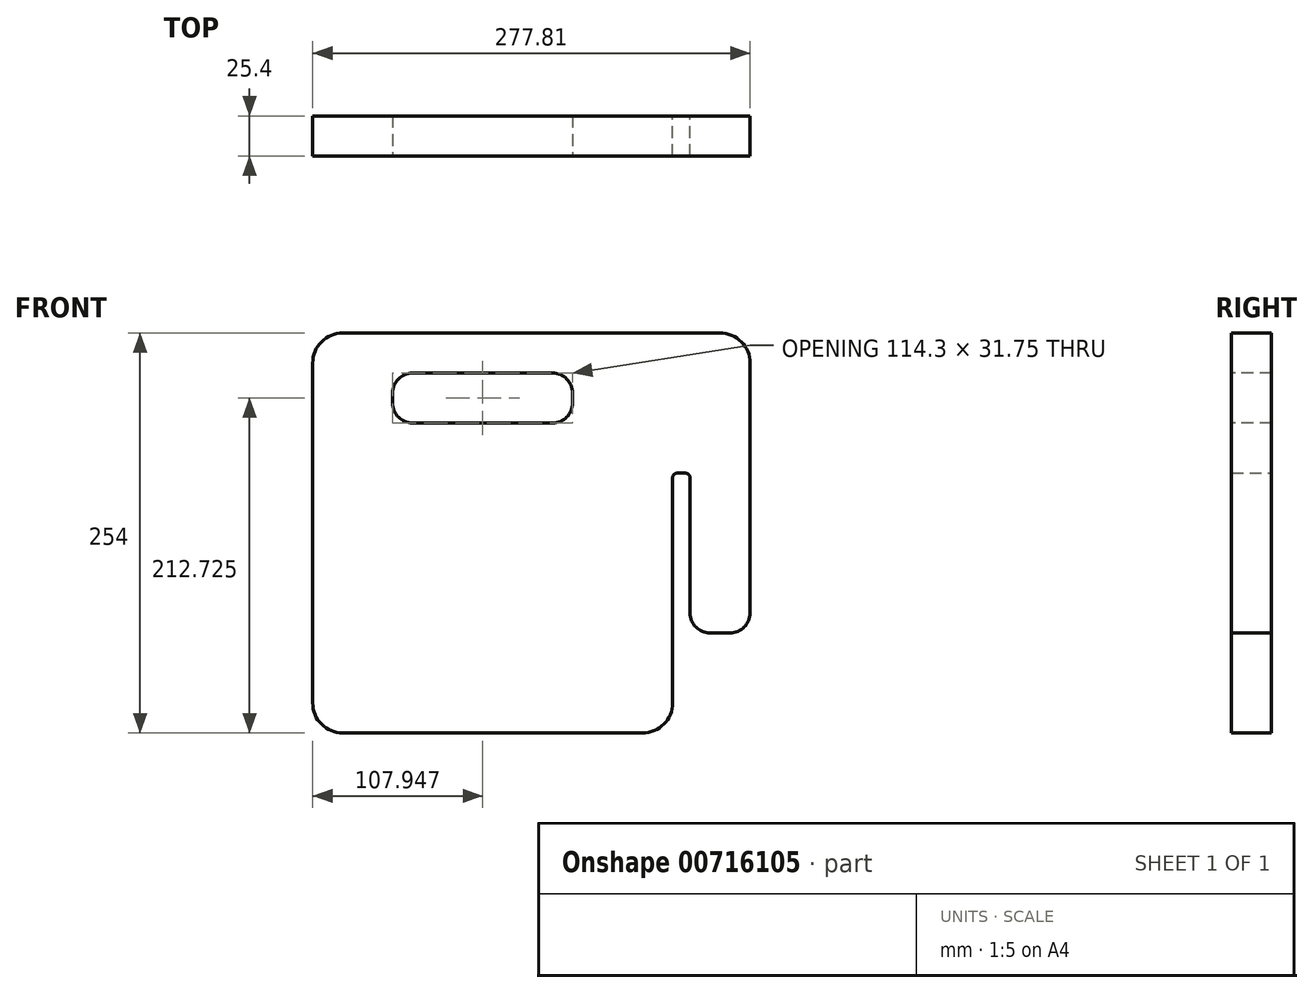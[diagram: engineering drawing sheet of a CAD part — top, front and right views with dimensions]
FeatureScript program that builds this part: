
annotation { "Feature Type Name" : "Feature", "Feature Type Description" : "" }
export const myFeature = defineFeature(function(context is Context, id is Id, definition is map)
    precondition{}
    {
        {
            var Q0;
            Q0=qCreatedBy(makeId("Front.planeOp"),FACE);
            var sketch = newSketch(context, id + "F0", { "sketchPlane" : qUnion([Q0])});
            skLineSegment(sketch, "E0.bottom", {"start": v(-69.16, 190.5) * mm, "end": v(170.55, 190.5) * mm});
            skLineSegment(sketch, "E0.left", {"start": v(-88.21, 171.45) * mm, "end": v(-88.21, -44.45) * mm});
            skLineSegment(sketch, "E1", {"start": v(148.32, 101.6) * mm, "end": v(143.56, 101.6) * mm});
            skLineSegment(sketch, "E2", {"start": v(140.39, 98.43) * mm, "end": v(140.39, -44.45) * mm});
            skLineSegment(sketch, "E3", {"start": v(-69.16, -63.5) * mm, "end": v(121.34, -63.5) * mm});
            skLineSegment(sketch, "E4", {"start": v(164.2, 0) * mm, "end": v(176.9, 0) * mm});
            skLineSegment(sketch, "E5", {"start": v(151.5, 12.7) * mm, "end": v(151.5, 98.43) * mm});
            skLineSegment(sketch, "E6", {"start": v(189.6, 12.7) * mm, "end": v(189.6, 171.45) * mm});
            skPoint(sketch, "E7.visualSharp", {"position": v(-88.21, 190.5) * mm});
            skArc(sketch, "E7.filletArc", {"start": v(-69.16, 190.5) * mm, "mid": v(-82.63, 184.92) * mm, "end": v(-88.21, 171.45) * mm});
            skPoint(sketch, "E8.visualSharp", {"position": v(-88.21, -63.5) * mm});
            skArc(sketch, "E8.filletArc", {"start": v(-88.21, -44.45) * mm, "mid": v(-82.63, -57.92) * mm, "end": v(-69.16, -63.5) * mm});
            skPoint(sketch, "E9.visualSharp", {"position": v(189.6, 190.5) * mm});
            skArc(sketch, "E9.filletArc", {"start": v(189.6, 171.45) * mm, "mid": v(184.02, 184.92) * mm, "end": v(170.55, 190.5) * mm});
            skPoint(sketch, "E10.visualSharp", {"position": v(189.6, 0) * mm});
            skArc(sketch, "E10.filletArc", {"start": v(176.9, 0) * mm, "mid": v(185.88, 3.72) * mm, "end": v(189.6, 12.7) * mm});
            skPoint(sketch, "E11.visualSharp", {"position": v(151.5, 0) * mm});
            skArc(sketch, "E11.filletArc", {"start": v(151.5, 12.7) * mm, "mid": v(155.22, 3.72) * mm, "end": v(164.2, 0) * mm});
            skPoint(sketch, "E12.visualSharp", {"position": v(140.39, -63.5) * mm});
            skArc(sketch, "E12.filletArc", {"start": v(121.34, -63.5) * mm, "mid": v(134.8, -57.92) * mm, "end": v(140.39, -44.45) * mm});
            skPoint(sketch, "E13.visualSharp", {"position": v(151.5, 101.6) * mm});
            skArc(sketch, "E13.filletArc", {"start": v(151.5, 98.43) * mm, "mid": v(150.57, 100.67) * mm, "end": v(148.32, 101.6) * mm});
            skPoint(sketch, "E14.visualSharp", {"position": v(140.39, 101.6) * mm});
            skArc(sketch, "E14.filletArc", {"start": v(143.56, 101.6) * mm, "mid": v(141.32, 100.67) * mm, "end": v(140.39, 98.43) * mm});
            skSolve(sketch);
        }
        {
            var Q0;
            Q0=makeQuery(id+"F0.imprint","IMPRINT",FACE,{"disambiguationData":[TD([[makeQuery(id+"F0.imprint","IMPRINT",EDGE,{"derivedFrom":sQuery(id+"F0.wireOp",EDGE,"E0.bottom")}),-1.0]])]});
            extrude(context, id + "F1", {"entities" : qUnion([Q0]), "depth" : 25.4 * mm, "offsetDistance" : 25.4 * mm});
        }
        {
            var Q0;
            Q0=makeQuery(id+"F1.opExtrude","CAP_FACE",FACE,{"disambiguationData":[OSD([sQuery(id+"F0.wireOp",EDGE,"E0.bottom"),sQuery(id+"F0.wireOp",EDGE,"E0.left"),sQuery(id+"F0.wireOp",EDGE,"E1"),sQuery(id+"F0.wireOp",EDGE,"E2"),sQuery(id+"F0.wireOp",EDGE,"E3"),sQuery(id+"F0.wireOp",EDGE,"E4"),sQuery(id+"F0.wireOp",EDGE,"E5"),sQuery(id+"F0.wireOp",EDGE,"E6"),sQuery(id+"F0.wireOp",EDGE,"E7.filletArc"),sQuery(id+"F0.wireOp",EDGE,"E8.filletArc"),sQuery(id+"F0.wireOp",EDGE,"E9.filletArc"),sQuery(id+"F0.wireOp",EDGE,"E10.filletArc"),sQuery(id+"F0.wireOp",EDGE,"E11.filletArc"),sQuery(id+"F0.wireOp",EDGE,"E12.filletArc"),sQuery(id+"F0.wireOp",EDGE,"E13.filletArc"),sQuery(id+"F0.wireOp",EDGE,"E14.filletArc")])],"isStart":false});
            var sketch = newSketch(context, id + "F2", { "sketchPlane" : qUnion([Q0])});
            skLineSegment(sketch, "E15.bottom", {"start": v(-24.71, 165.1) * mm, "end": v(64.19, 165.1) * mm});
            skLineSegment(sketch, "E15.top", {"start": v(-24.71, 133.35) * mm, "end": v(64.19, 133.35) * mm});
            skLineSegment(sketch, "E15.left", {"start": v(-37.41, 152.4) * mm, "end": v(-37.41, 146.05) * mm});
            skLineSegment(sketch, "E15.right", {"start": v(76.89, 152.4) * mm, "end": v(76.89, 146.05) * mm});
            skPoint(sketch, "E16.visualSharp", {"position": v(-37.41, 165.1) * mm});
            skArc(sketch, "E16.filletArc", {"start": v(-24.71, 165.1) * mm, "mid": v(-33.7, 161.38) * mm, "end": v(-37.41, 152.4) * mm});
            skPoint(sketch, "E17.visualSharp", {"position": v(-37.41, 133.35) * mm});
            skArc(sketch, "E17.filletArc", {"start": v(-37.41, 146.05) * mm, "mid": v(-33.7, 137.07) * mm, "end": v(-24.71, 133.35) * mm});
            skPoint(sketch, "E18.visualSharp", {"position": v(76.89, 133.35) * mm});
            skArc(sketch, "E18.filletArc", {"start": v(64.19, 133.35) * mm, "mid": v(73.17, 137.07) * mm, "end": v(76.89, 146.05) * mm});
            skPoint(sketch, "E19.visualSharp", {"position": v(76.89, 165.1) * mm});
            skArc(sketch, "E19.filletArc", {"start": v(76.89, 152.4) * mm, "mid": v(73.17, 161.38) * mm, "end": v(64.19, 165.1) * mm});
            skSolve(sketch);
        }
        {
            var Q0;
            Q0=makeQuery(id+"F2.imprint","IMPRINT",FACE,{"disambiguationData":[TD([[makeQuery(id+"F2.imprint","IMPRINT",EDGE,{"derivedFrom":sQuery(id+"F2.wireOp",EDGE,"E15.bottom")}),-1.0]])]});
            extrude(context, id + "F3", {"entities" : qUnion([Q0]), "operationType" : NewBodyOperationType.REMOVE, "endBound" : BoundingType.THROUGH_ALL, "oppositeDirection" : true, "depth" : 25.4 * mm, "offsetDistance" : 25.4 * mm});
        }
    });
